# Revit family: Door_FTS CD_The Sliding Door Company_1.5F 3-Panel Triple Track (Regular)
name_source: partatom
category: Doors
units: mm (PartAtom-declared; Revit-internal decimal feet)

## family parameters
Always vertical = Yes
Cut with Voids When Loaded = No
Host = Wall
OmniClass Number = 23.30.10.00
OmniClass Title = Doors
Room Calculation Point = No
Shared = No

## types (1)
- FTS Closet Divider - 1.5F 3 Panel 3 Track - ABC/CBA
    1 1/2" Frame (No Support Dividers) = Max. H=108 in., Max. W=147 in. (50 in. panel width)
    Analytic Construction = <None>
    Configuration = ABC/CBA Configuration
    Construction Type = Top Mounted, Regular Bottom Track
    Description = 1.5 Frame 3 Panel System with Triple Track (Regular)
    Finished Opening Height = 108"
    Finished Opening Width = 147"
    Function = Interior
    Glass Thickness = Available in: 5mm Tempered, 7mm,10mm,11mm Laminated Glass
    Height = 108"
    Limitations = Panel Width x System Height cannot exceed 7,400 square inches
    Manufacturer = The Sliding Door Company
    Model = FTS Closet Divider - Full Height System
    Panel Height = 105 3/4"
    Panel Width = 50"
    Rough Height = 108 5/8"
    Rough Width = 148 1/4"
    Stile/Rail = 1 1/2"
    Thickness = 1 1/4"
    URL = https://www.slidingdoorco.com
    Wall Closure = By host
    Width = 147"

## geometry (parser evidence)
native form markers: Blend x3, Sweep x5
no freeform markers — native parametric forms only
